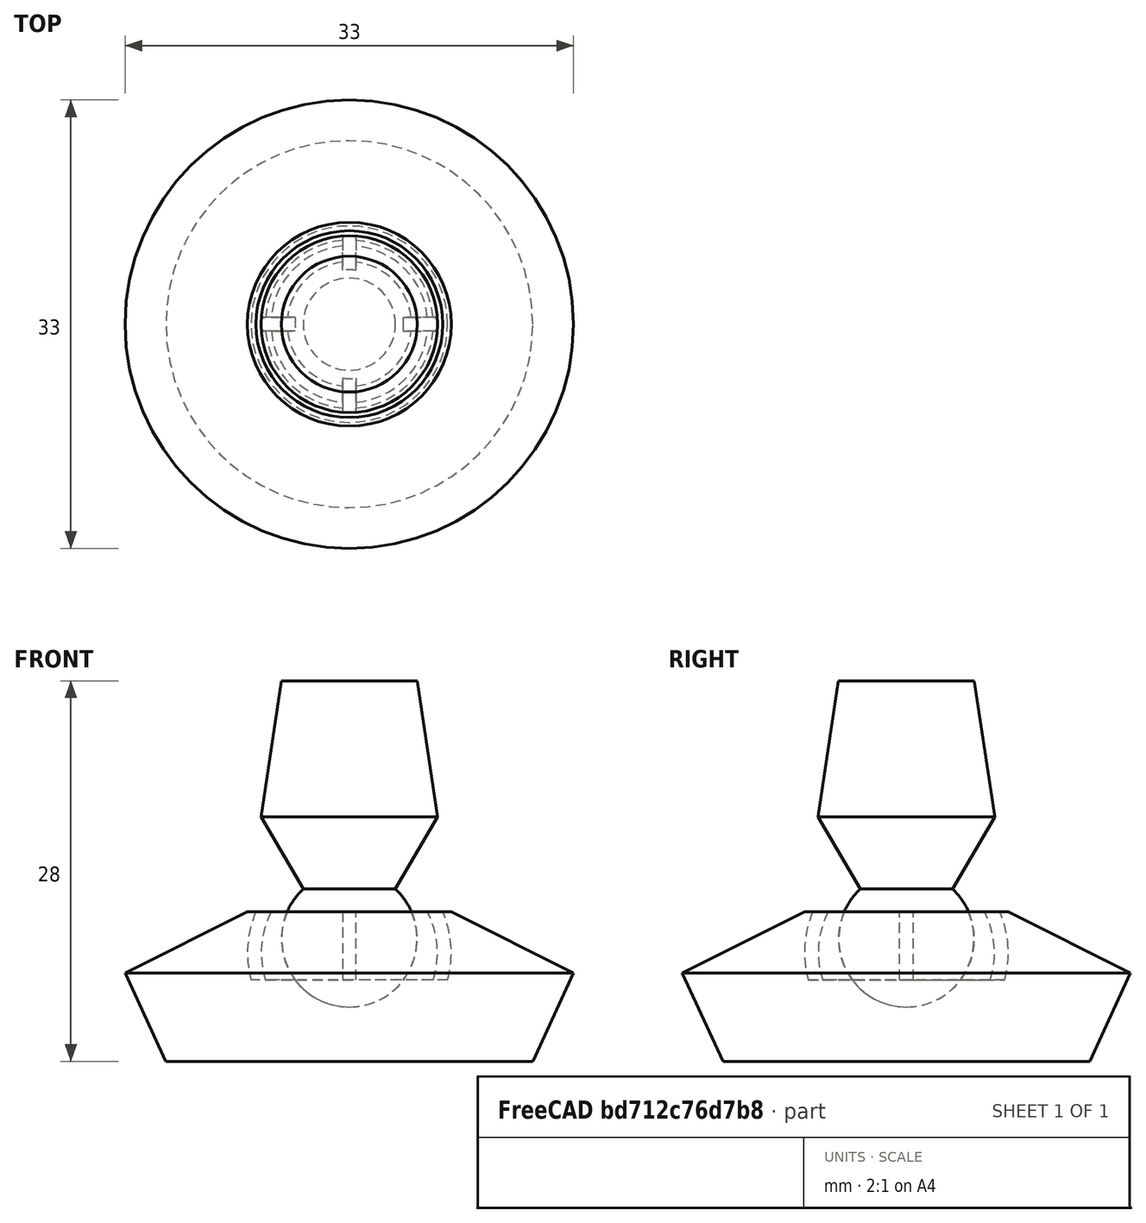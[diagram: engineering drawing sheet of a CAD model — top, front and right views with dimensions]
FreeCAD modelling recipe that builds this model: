
FCSTD DOCUMENT  (FreeCAD 0.14R3703 (Git))
Label: Eames Lounge Foot v2
License: CC-BY 3.0
LicenseURL: http://creativecommons.org/licenses/by/3.0/
objects: Part::Cone×4, Part::Sphere×4, Part::MultiFuse×4, Part::Cylinder×3, Part::Cut×3
note: 18 computed .brp shape members not serialized (recipe doc carries the construction recipe); baked Part::Feature solids carry a one-line shape summary decoded from their .brp

FEATURE [Part::Cone] Cone
  Angle = 360
  Height = 6
  Placement = pos=(0,0,11) rot=(0,0,1;0rad)
  Radius1 = 3
  Radius2 = 6.5
FEATURE [Part::Sphere] Sphere
  Angle1 = -90
  Angle2 = 90
  Angle3 = 360
  Placement = pos=(0,0,8) rot=(0,0,1;0rad)
  Radius = 5
FEATURE [Part::Cone] Cone001
  Angle = 360
  Height = 10
  Placement = pos=(0,0,17) rot=(0,0,1;0rad)
  Radius1 = 6.5
  Radius2 = 5
FEATURE [Part::Cone] Cone002  label="Cone1"
  Angle = 360
  Height = 6.5
  Radius1 = 13.5
  Radius2 = 16.5
FEATURE [Part::Cone] Cone003  label="Cone2"
  Angle = 360
  Height = 4.5
  Placement = pos=(0,0,6.5) rot=(0,0,1;0rad)
  Radius1 = 16.5
  Radius2 = 7.5
FEATURE [Part::MultiFuse] Fusion  label="Shaft"
  Placement = pos=(0,0,1) rot=(0,0,1;0rad)
  Shapes = -> [Sphere,Cone001,Cone]
FEATURE [Part::MultiFuse] Fusion001  label="Foot Uncut"
  Shapes = -> [Cone002,Cone003]
FEATURE [Part::Sphere] Sphere002
  Angle1 = -90
  Angle2 = 90
  Angle3 = 360
  Placement = pos=(0,0,7) rot=(0,0,1;0rad)
  Radius = 7.5
FEATURE [Part::Cylinder] Cylinder
  Angle = 360
  Height = 6
  Placement = pos=(0,0,-1) rot=(0,0,1;0rad)
  Radius = 10
FEATURE [Part::Sphere] Sphere004
  Angle1 = -90
  Angle2 = 90
  Angle3 = 360
  Placement = pos=(0,0,7) rot=(0,0,1;0rad)
  Radius = 6.5
FEATURE [Part::Cylinder] Cylinder001
  Angle = 360
  Height = 1
  Placement = pos=(-0.5,0,7) rot=(0,1,0;1.5708rad)
  Radius = 6.5
FEATURE [Part::Cylinder] Cylinder002
  Angle = 360
  Height = 1
  Placement = pos=(0,0.5,7) rot=(1,0,0;1.5708rad)
  Radius = 6.5
FEATURE [Part::Cut] Cut001
  Base = -> Sphere002
  Tool = -> Sphere004
FEATURE [Part::MultiFuse] Fusion002
  Shapes = -> [Cylinder001,Cylinder002,Cut001]
FEATURE [Part::Sphere] Sphere001
  Angle1 = -90
  Angle2 = 90
  Angle3 = 360
  Placement = pos=(0,0,8) rot=(0,0,1;0rad)
  Radius = 5
FEATURE [Part::Cut] Cut
  Base = -> Fusion002
  Tool = -> Cylinder
FEATURE [Part::MultiFuse] Fusion003  label="Cutout"
  Placement = pos=(0,0,1) rot=(0,0,1;0rad)
  Shapes = -> [Sphere001,Cut]
FEATURE [Part::Cut] Cut002  label="Foot Unfilleted"
  Base = -> Fusion001
  Tool = -> Fusion003
